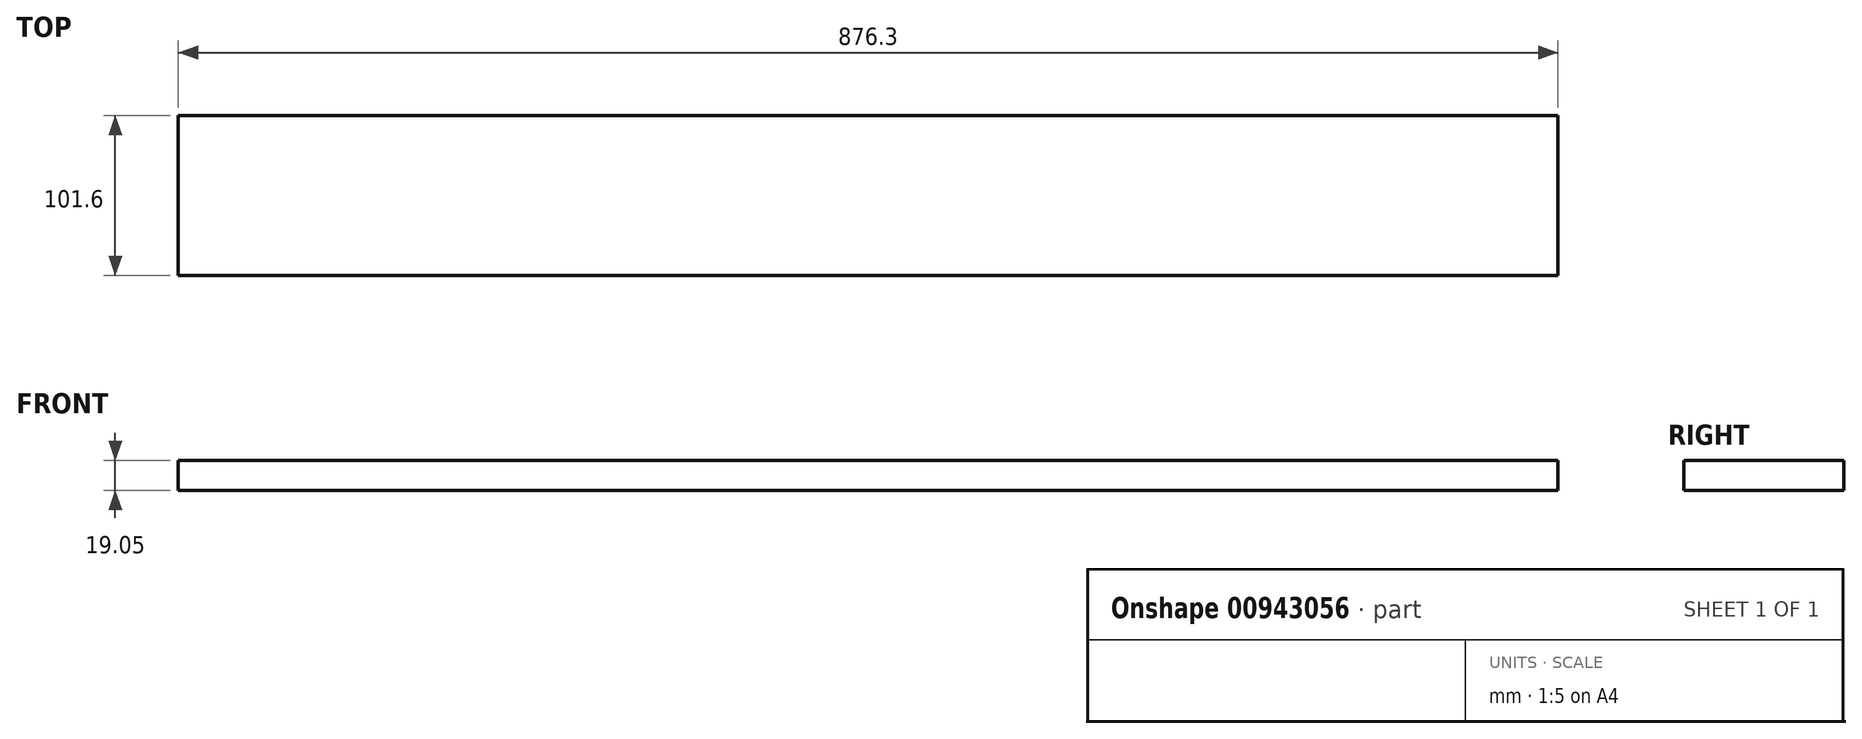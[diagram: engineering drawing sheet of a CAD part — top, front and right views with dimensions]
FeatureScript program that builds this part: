
annotation { "Feature Type Name" : "Feature", "Feature Type Description" : "" }
export const myFeature = defineFeature(function(context is Context, id is Id, definition is map)
    precondition{}
    {
        {
            var Q0;
            Q0=qCreatedBy(makeId("Top.planeOp"),FACE);
            var sketch = newSketch(context, id + "F0", { "sketchPlane" : qUnion([Q0])});
            skLineSegment(sketch, "E0.bottom", {"start": v(0, 0) * mm, "end": v(876.3, 0) * mm});
            skLineSegment(sketch, "E0.top", {"start": v(0, 101.6) * mm, "end": v(876.3, 101.6) * mm});
            skLineSegment(sketch, "E0.left", {"start": v(0, 0) * mm, "end": v(0, 101.6) * mm});
            skLineSegment(sketch, "E0.right", {"start": v(876.3, 0) * mm, "end": v(876.3, 101.6) * mm});
            skSolve(sketch);
        }
        {
            var Q0;
            Q0=makeQuery(id+"F0.imprint","IMPRINT",FACE,{"disambiguationData":[TD([[makeQuery(id+"F0.imprint","IMPRINT",EDGE,{"derivedFrom":sQuery(id+"F0.wireOp",EDGE,"E0.bottom")}),1.0]])]});
            extrude(context, id + "F1", {"entities" : qUnion([Q0]), "depth" : 19.05 * mm, "offsetDistance" : 25.4 * mm});
        }
    });
